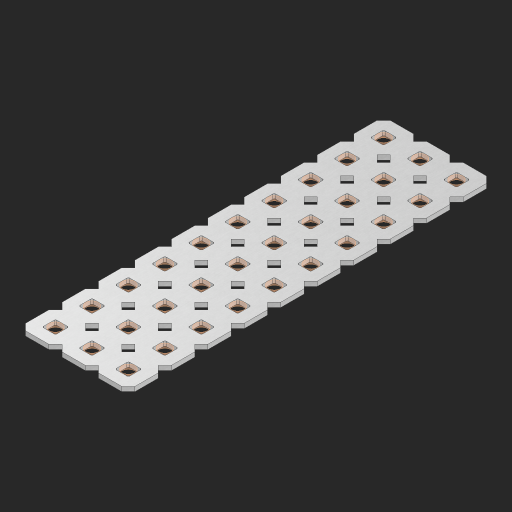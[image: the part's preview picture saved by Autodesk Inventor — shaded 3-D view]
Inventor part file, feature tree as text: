
AUTODESK INVENTOR PART (.ipt)
format: ipt  version: 2023 (Build 270158000, 158)  size: 636,416 bytes
history: native  units: in
note: dims shown in document units (in); Inventor stores cm internally (conversion verified against a paired STEP export)
features: other x31, extrude x29, sketch x2, pattern_linear x1
ambient origin geometry x8: Origin, YZ Plane, XZ Plane, XY Plane, X Axis, Y Axis, Z Axis, Center Point
bodies: Solid1 (feature_tree), Body (feature_tree)
feature tree (63):
  pattern_linear  "Rectangular Pattern1"  Spacing1=0.09in  [1 undecoded]
  sketch  "Sketch1"  dims[d1=0.5in]
  sketch  "Sketch2"  dims[d2=0.182in d3=0.09in d4=0.09in d5=0.09in d6=0.09in d7=0.09in d8=0.09in d9=0.09in d10=0.09in d11=0.02in d13=0.0in d14=0.172in d15=0.0625in d16=0.0in d19=0.5in d22=0.5in]
  other  "Srf1"
  other  "Srf126"
  other  "Srf127"
  other  "Srf128"
  other  "Srf129"
  other  "Srf130"
  other  "Srf131"
  other  "Srf250"
  other  "Srf251"
  other  "Srf252"
  other  "Srf268"
  other  "Srf269"
  other  "Srf270"
  other  "Srf271"
  other  "Srf272"
  other  "Srf273"
  other  "Srf274"
  other  "Srf275"
  other  "Srf276"
  other  "Srf277"
  other  "Srf293"
  other  "Srf294"
  other  "Srf295"
  other  "Srf296"
  other  "Srf297"
  other  "Srf298"
  other  "Srf299"
  other  "Srf300"
  other  "Srf301"
  other  "Srf302"
  other  "Circle"
  extrude  "ExtrusionSrf126"  Depth=0.09in
  extrude  "ExtrusionSrf127"  Depth=0.09in
  extrude  "ExtrusionSrf128"  Depth=0.09in
  extrude  "ExtrusionSrf129"  Depth=0.09in
  extrude  "ExtrusionSrf130"  Depth=0.09in
  extrude  "ExtrusionSrf131"  Depth=0.09in
  extrude  "ExtrusionSrf250"  Depth=0.09in
  extrude  "ExtrusionSrf251"  Depth=0.02in
  extrude  "ExtrusionSrf252"  TaperAngle=0.0deg  [1 undecoded]
  extrude  "ExtrusionSrf268"  Depth=0.5in
  extrude  "ExtrusionSrf269"  Depth=0.0625in TaperAngle=0.0deg
  extrude  "ExtrusionSrf270"  Depth=0.5in
  extrude  "ExtrusionSrf271"  Depth=0.5in
  extrude  "ExtrusionSrf272"  [1 undecoded]
  extrude  "ExtrusionSrf273"  [1 undecoded]
  extrude  "ExtrusionSrf274"  [1 undecoded]
  extrude  "ExtrusionSrf275"  [1 undecoded]
  extrude  "ExtrusionSrf276"  [1 undecoded]
  extrude  "ExtrusionSrf277"  [1 undecoded]
  extrude  "ExtrusionSrf293"  [1 undecoded]
  extrude  "ExtrusionSrf294"  [1 undecoded]
  extrude  "ExtrusionSrf295"  [1 undecoded]
  extrude  "ExtrusionSrf296"  [1 undecoded]
  extrude  "ExtrusionSrf297"  [1 undecoded]
  extrude  "ExtrusionSrf298"  [1 undecoded]
  extrude  "ExtrusionSrf299"  [1 undecoded]
  extrude  "ExtrusionSrf300"  [1 undecoded]
  extrude  "ExtrusionSrf301"  [1 undecoded]
  extrude  "ExtrusionSrf302"  [1 undecoded]
note: 18 required parameter values undecoded (feature->parameter linkage not recoverable at this tier; creation-order binding heuristic only, values carry confidence <= 0.55)
